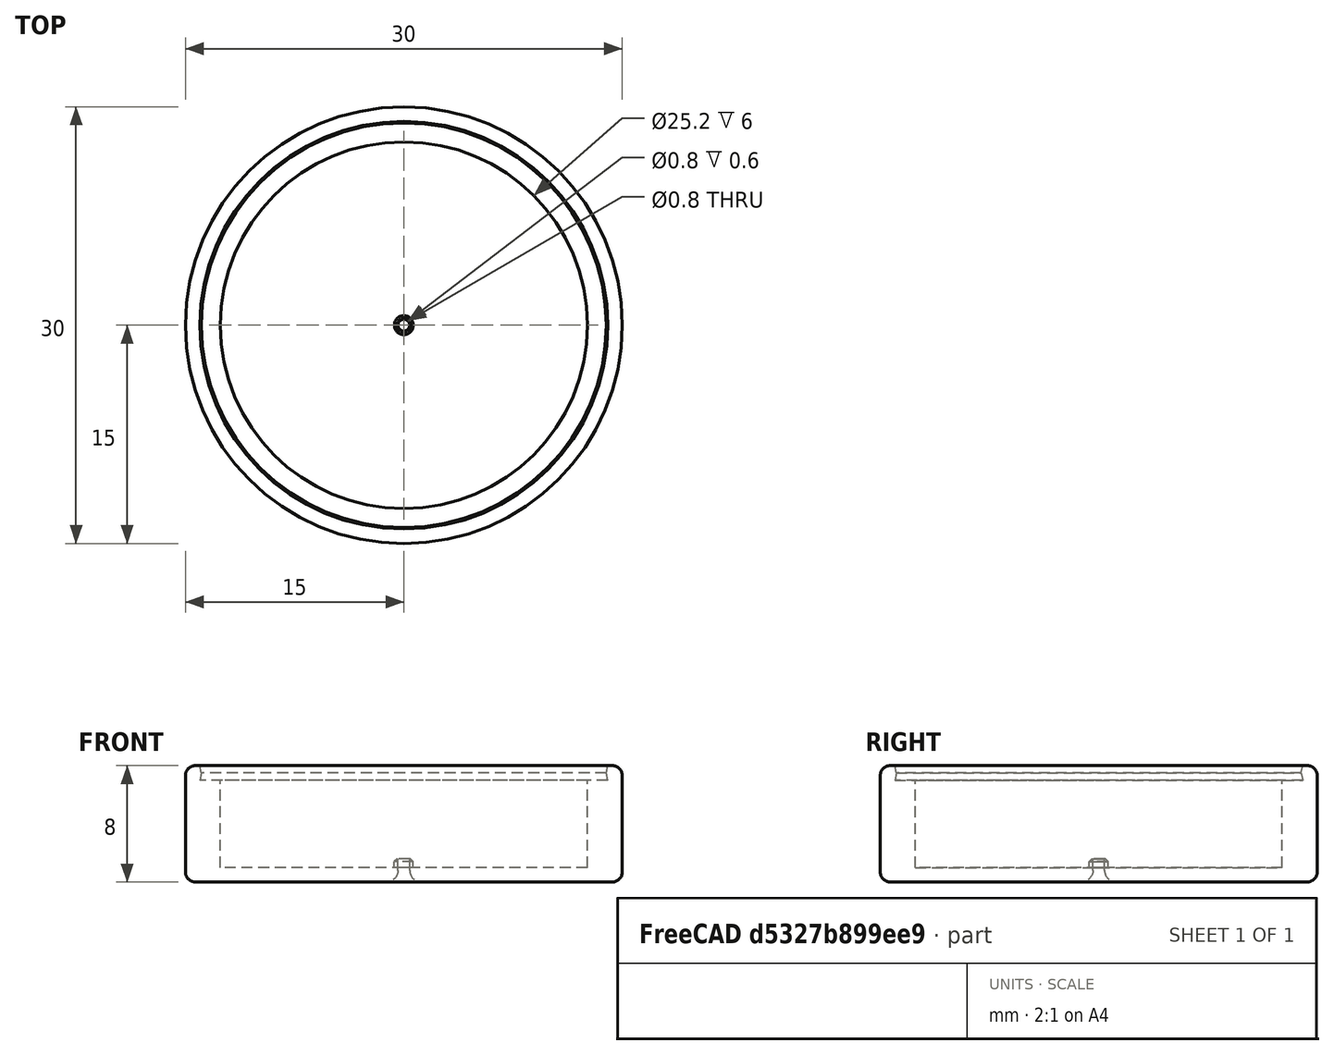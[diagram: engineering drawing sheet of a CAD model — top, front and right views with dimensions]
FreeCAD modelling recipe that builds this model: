
FCSTD DOCUMENT  (FreeCAD 0.18R16117 (Git))
Label: niklas_2
License: All rights reserved
LicenseURL: http://en.wikipedia.org/wiki/All_rights_reserved
objects: Part::Cylinder×8, Part::Cut×6, Part::Fillet×3, Part::MultiFuse×2, Part::Cone×2, Part::Chamfer×1
note: 22 computed .brp shape members not serialized (recipe doc carries the construction recipe); baked Part::Feature solids carry a one-line shape summary decoded from their .brp

FEATURE [Part::Cylinder] Cylinder
  Angle = 360
  AttacherType = Attacher::AttachEngine3D
  Height = 8
  Radius = 15
FEATURE [Part::Cylinder] Cylinder001
  Angle = 360
  AttacherType = Attacher::AttachEngine3D
  Height = 8
  Radius = 12.6
FEATURE [Part::Cut] Cut
  Base = -> Cylinder
  Tool = -> Cylinder001
FEATURE [Part::Cylinder] Cylinder002
  Angle = 360
  AttacherType = Attacher::AttachEngine3D
  Height = 1
  Radius = 15
FEATURE [Part::MultiFuse] Fusion
  Shapes = -> [Cylinder002,Cut]
FEATURE [Part::Cylinder] Cylinder005
  Angle = 360
  AttacherType = Attacher::AttachEngine3D
  Height = 1
  Radius = 0.4
FEATURE [Part::Cut] Cut001
  Base = -> Fusion
  Tool = -> Cylinder005
FEATURE [Part::Cylinder] Cylinder004
  Angle = 360
  AttacherType = Attacher::AttachEngine3D
  Height = 0.6
  Placement = pos=(0,0,1) rot=(0,0,1;0rad)
  Radius = 0.4
FEATURE [Part::Cylinder] Cylinder003
  Angle = 360
  AttacherType = Attacher::AttachEngine3D
  Height = 0.6
  Placement = pos=(0,0,1) rot=(0,0,1;0rad)
  Radius = 0.65
FEATURE [Part::Cut] Cut002
  Base = -> Cylinder003
  Tool = -> Cylinder004
FEATURE [Part::Chamfer] Chamfer
  Base = -> Cut002
  Edges = 1 edges r=0.2: [Edge1]
FEATURE [Part::Cylinder] Cylinder006
  Angle = 360
  AttacherType = Attacher::AttachEngine3D
  Height = 1
  Placement = pos=(0,0,7) rot=(0,0,1;0rad)
  Radius = 14
FEATURE [Part::Cut] Cut003
  Base = -> Cut001
  Tool = -> Cylinder006
FEATURE [Part::Cone] Cone
  Angle = 360
  AttacherType = Attacher::AttachEngine3D
  Height = 1
  Placement = pos=(0,0,7) rot=(0,0,1;0rad)
  Radius1 = 14
  Radius2 = 13.8
FEATURE [Part::Cylinder] Cylinder007
  Angle = 360
  AttacherType = Attacher::AttachEngine3D
  Height = 1
  Placement = pos=(0,0,7) rot=(0,0,1;0rad)
  Radius = 14
FEATURE [Part::Cut] Cut004
  Base = -> Cylinder007
  Tool = -> Cone
FEATURE [Part::Cone] Cone001
  Angle = 360
  AttacherType = Attacher::AttachEngine3D
  Height = 1
  Placement = pos=(0,0,7) rot=(0,0,1;0rad)
  Radius1 = 13.8
  Radius2 = 14
FEATURE [Part::Cut] Cut005
  Base = -> Cut004
  Tool = -> Cone001
FEATURE [Part::Fillet] Fillet
  Base = -> Cut003
  Edges = 1 edges r=0.7: [Edge5]
FEATURE [Part::Fillet] Fillet001
  Base = -> Fillet
  Edges = 1 edges r=0.7: [Edge7]
FEATURE [Part::Fillet] Fillet002
  Base = -> Fillet001
  Edges = 1 edges r=0.8: [Edge11]
FEATURE [Part::MultiFuse] Fusion001
  Shapes = -> [Chamfer,Cut005,Fillet002]
